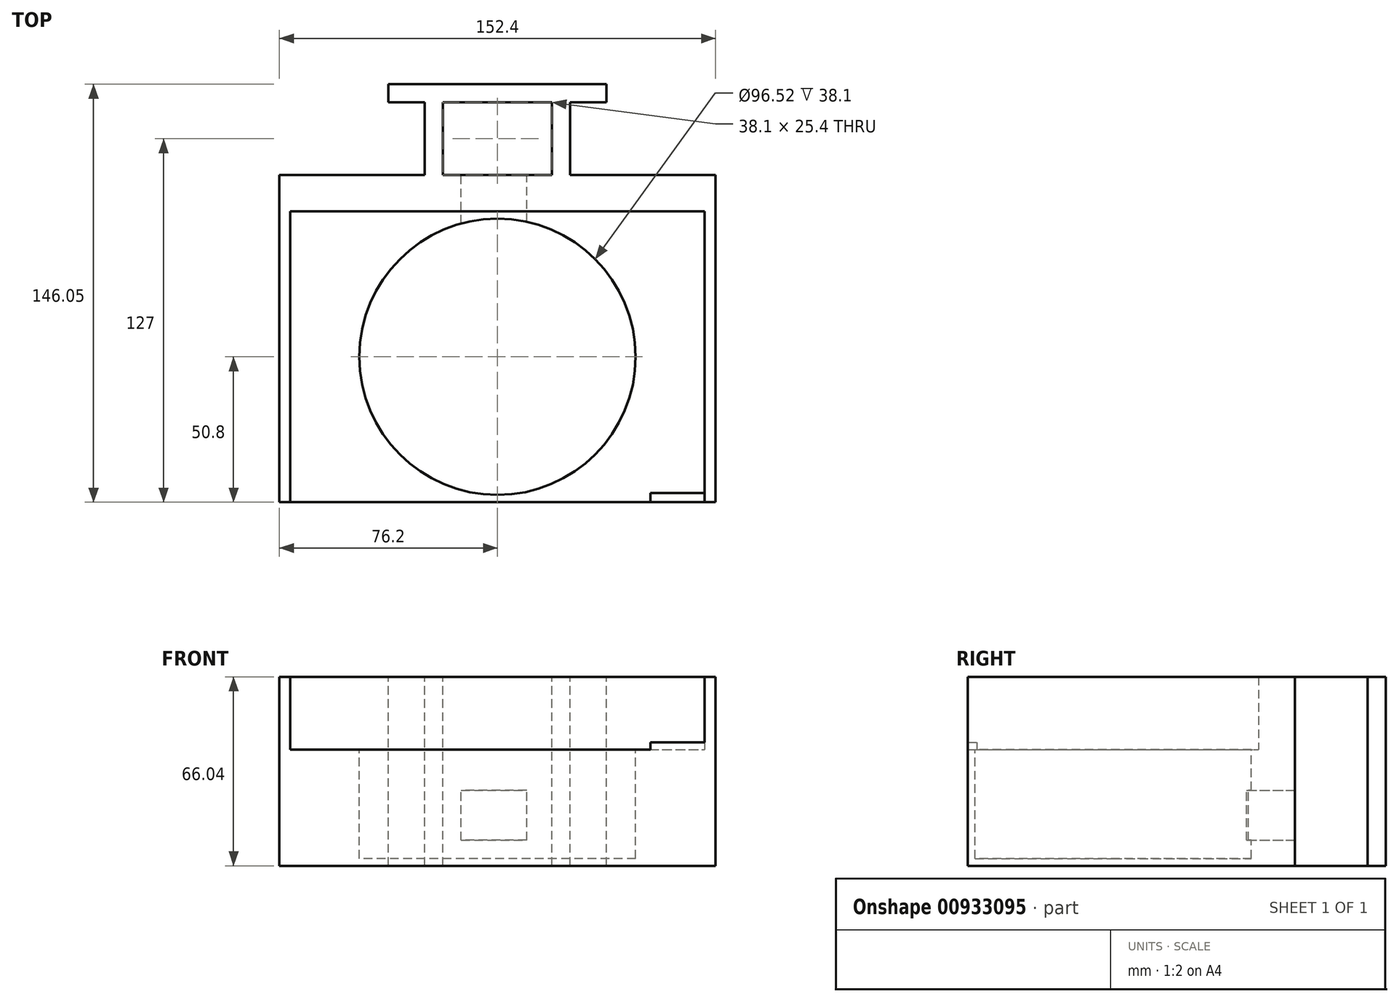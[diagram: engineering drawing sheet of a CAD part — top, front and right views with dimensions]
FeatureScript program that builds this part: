
annotation { "Feature Type Name" : "Feature", "Feature Type Description" : "" }
export const myFeature = defineFeature(function(context is Context, id is Id, definition is map)
    precondition{}
    {
        {
            var Q0;
            Q0=qCreatedBy(makeId("Top.planeOp"),FACE);
            var sketch = newSketch(context, id + "F0", { "sketchPlane" : qUnion([Q0])});
            skLineSegment(sketch, "E0.bottom", {"start": v(-76.2, 57.15) * mm, "end": v(76.2, 57.15) * mm});
            skLineSegment(sketch, "E0.top", {"start": v(-76.2, -57.15) * mm, "end": v(76.2, -57.15) * mm});
            skLineSegment(sketch, "E0.left", {"start": v(-76.2, 57.15) * mm, "end": v(-76.2, -57.15) * mm});
            skLineSegment(sketch, "E0.right", {"start": v(76.2, 57.15) * mm, "end": v(76.2, -57.15) * mm});
            skSolve(sketch);
        }
        {
            var Q0;
            Q0=makeQuery(id+"F0.imprint","IMPRINT",FACE,{"disambiguationData":[TD([[makeQuery(id+"F0.imprint","IMPRINT",EDGE,{"derivedFrom":sQuery(id+"F0.wireOp",EDGE,"E0.bottom")}),-1.0]])]});
            extrude(context, id + "F1", {"entities" : qUnion([Q0]), "depth" : 40.64 * mm, "offsetDistance" : 25.4 * mm});
        }
        {
            var Q0;
            Q0=makeQuery(id+"F1.opExtrude","CAP_FACE",FACE,{"disambiguationData":[OSD([sQuery(id+"F0.wireOp",EDGE,"E0.bottom"),sQuery(id+"F0.wireOp",EDGE,"E0.top"),sQuery(id+"F0.wireOp",EDGE,"E0.left"),sQuery(id+"F0.wireOp",EDGE,"E0.right")])],"isStart":false});
            var sketch = newSketch(context, id + "F2", { "sketchPlane" : qUnion([Q0])});
            skLineSegment(sketch, "E1.trimOffspring", {"start": v(-72.4, 44.45) * mm, "end": v(72.4, 44.45) * mm});
            skLineSegment(sketch, "E2", {"start": v(76.2, 57.15) * mm, "end": v(-76.2, 57.15) * mm});
            skLineSegment(sketch, "E3.bottom", {"start": v(76.2, -57.15) * mm, "end": v(72.4, -57.15) * mm});
            skLineSegment(sketch, "E3.left", {"start": v(76.2, -57.15) * mm, "end": v(76.2, 57.15) * mm});
            skLineSegment(sketch, "E4.bottom", {"start": v(-76.2, -57.15) * mm, "end": v(-72.4, -57.15) * mm});
            skLineSegment(sketch, "E4.left", {"start": v(-76.2, -57.15) * mm, "end": v(-76.2, 57.15) * mm});
            skLineSegment(sketch, "E4.right", {"start": v(-72.4, -57.15) * mm, "end": v(-72.4, 44.45) * mm});
            skLineSegment(sketch, "E5", {"start": v(72.4, -57.15) * mm, "end": v(72.4, 44.45) * mm});
            skSolve(sketch);
        }
        {
            var Q0;
            {var subQ0=sQuery(id+"F2.wireOp",EDGE,"OgKXzPdw-eDsp-d21L-xpKS-83sbPqBPL3Dp.bottom");Q0=makeQuery(id+"F2.imprint","IMPRINT",FACE,{"disambiguationData":[TD([[makeQuery(id+"F2.imprint","IMPRINT",EDGE,{"derivedFrom":subQ0}),1.0]])]});}
            var Q1;
            {var subQ0=sQuery(id+"F2.wireOp",EDGE,"E1.trimOffspring");Q1=makeQuery(id+"F2.imprint","IMPRINT",FACE,{"disambiguationData":[TD([[makeQuery(id+"F2.imprint","IMPRINT",EDGE,{"derivedFrom":subQ0}),1.0]])]});}
            var Q2;
            {var subQ0=sQuery(id+"F2.wireOp",EDGE,"0cbdea43-ffa5-4f05-8e79-97b593feb2ee.trimOffspring");Q2=makeQuery(id+"F2.imprint","IMPRINT",FACE,{"disambiguationData":[TD([[makeQuery(id+"F2.imprint","IMPRINT",EDGE,{"derivedFrom":subQ0}),-1.0]])]});}
            var Q3;
            {var subQ0=sQuery(id+"F2.wireOp",EDGE,"OgKXzPdw-eDsp-d21L-xpKS-83sbPqBPL3Dp.top");Q3=makeQuery(id+"F2.imprint","IMPRINT",FACE,{"disambiguationData":[TD([[makeQuery(id+"F2.imprint","IMPRINT",EDGE,{"derivedFrom":subQ0}),-1.0]])]});}
            extrude(context, id + "F3", {"entities" : qUnion([Q0, Q1, Q2, Q3]), "operationType" : NewBodyOperationType.ADD, "depth" : 25.4 * mm, "offsetDistance" : 25.4 * mm});
        }
        {
            var Q0;
            Q0=makeQuery(id+"F1.opExtrude","CAP_FACE",FACE,{"disambiguationData":[OSD([sQuery(id+"F0.wireOp",EDGE,"E0.bottom"),sQuery(id+"F0.wireOp",EDGE,"E0.top"),sQuery(id+"F0.wireOp",EDGE,"E0.left"),sQuery(id+"F0.wireOp",EDGE,"E0.right")])],"isStart":false});
            var sketch = newSketch(context, id + "F4", { "sketchPlane" : qUnion([Q0])});
            skCircle(sketch, "E6", {"center": v(0, -6.35) * mm, "radius": 48.26 * mm});
            skSolve(sketch);
        }
        {
            var Q0;
            Q0=qSketchRegion(id+"F4",true);
            extrude(context, id + "F5", {"entities" : qUnion([Q0]), "operationType" : NewBodyOperationType.REMOVE, "oppositeDirection" : true, "depth" : 38.1 * mm, "offsetDistance" : 25.4 * mm});
        }
        {
            var Q0;
            Q0=makeQuery(id+"F3.opExtrude","CAP_FACE",FACE,{"disambiguationData":[OSD([sQuery(id+"F2.wireOp",EDGE,"E1.trimOffspring"),sQuery(id+"F2.wireOp",EDGE,"E2"),sQuery(id+"F2.wireOp",EDGE,"E3.bottom"),sQuery(id+"F2.wireOp",EDGE,"E3.left"),sQuery(id+"F2.wireOp",EDGE,"E4.bottom"),sQuery(id+"F2.wireOp",EDGE,"E4.left"),sQuery(id+"F2.wireOp",EDGE,"E4.right"),sQuery(id+"F2.wireOp",EDGE,"E5")])],"isStart":false});
            var sketch = newSketch(context, id + "F6", { "sketchPlane" : qUnion([Q0])});
            skLineSegment(sketch, "E7.bottom", {"start": v(-25.4, 57.15) * mm, "end": v(25.4, 57.15) * mm});
            skLineSegment(sketch, "E7.top", {"start": v(-25.4, 82.55) * mm, "end": v(25.4, 82.55) * mm});
            skLineSegment(sketch, "E7.left", {"start": v(-25.4, 57.15) * mm, "end": v(-25.4, 82.55) * mm});
            skLineSegment(sketch, "E7.right", {"start": v(25.4, 57.15) * mm, "end": v(25.4, 82.55) * mm});
            skLineSegment(sketch, "E8.bottom", {"start": v(-38.1, 88.9) * mm, "end": v(38.1, 88.9) * mm});
            skLineSegment(sketch, "E8.top", {"start": v(-38.1, 82.55) * mm, "end": v(38.1, 82.55) * mm});
            skLineSegment(sketch, "E8.left", {"start": v(-38.1, 88.9) * mm, "end": v(-38.1, 82.55) * mm});
            skLineSegment(sketch, "E8.right", {"start": v(38.1, 88.9) * mm, "end": v(38.1, 82.55) * mm});
            skSolve(sketch);
        }
        {
            var Q0;
            Q0=makeQuery(id+"F6.imprint","IMPRINT",FACE,{"disambiguationData":[TD([[makeQuery(id+"F6.imprint","IMPRINT",EDGE,{"derivedFrom":sQuery(id+"F6.wireOp",EDGE,"E7.bottom")}),1.0]])]});
            var Q1;
            Q1=makeQuery(id+"F6.imprint","IMPRINT",FACE,{"disambiguationData":[TD([[makeQuery(id+"F6.imprint","IMPRINT",EDGE,{"derivedFrom":sQuery(id+"F6.wireOp",EDGE,"E8.bottom")}),-1.0]])]});
            extrude(context, id + "F7", {"entities" : qUnion([Q0, Q1]), "operationType" : NewBodyOperationType.ADD, "oppositeDirection" : true, "depth" : 66.04 * mm, "offsetDistance" : 25.4 * mm});
        }
        {
            var Q0;
            Q0=makeQuery(id+"F7.boolean.opBoolean","MERGE",FACE,{"derivedFrom":[makeQuery(id+"F3.opExtrude","CAP_FACE",FACE,{"disambiguationData":[OSD([sQuery(id+"F2.wireOp",EDGE,"E1.trimOffspring"),sQuery(id+"F2.wireOp",EDGE,"E2"),sQuery(id+"F2.wireOp",EDGE,"E3.bottom"),sQuery(id+"F2.wireOp",EDGE,"E3.left"),sQuery(id+"F2.wireOp",EDGE,"E4.bottom"),sQuery(id+"F2.wireOp",EDGE,"E4.left"),sQuery(id+"F2.wireOp",EDGE,"E4.right"),sQuery(id+"F2.wireOp",EDGE,"E5")])],"isStart":false}),makeQuery(id+"F7.opExtrude","CAP_FACE",FACE,{"disambiguationData":[OSD([sQuery(id+"F6.wireOp",EDGE,"E7.bottom"),sQuery(id+"F6.wireOp",EDGE,"E7.left"),sQuery(id+"F6.wireOp",EDGE,"E7.right"),sQuery(id+"F6.wireOp",EDGE,"E8.bottom"),sQuery(id+"F6.wireOp",EDGE,"E8.top"),sQuery(id+"F6.wireOp",EDGE,"E8.left"),sQuery(id+"F6.wireOp",EDGE,"E8.right")])],"isStart":true})]});
            var sketch = newSketch(context, id + "F8", { "sketchPlane" : qUnion([Q0])});
            skLineSegment(sketch, "E9.bottom", {"start": v(-19.05, 82.55) * mm, "end": v(19.05, 82.55) * mm});
            skLineSegment(sketch, "E9.top", {"start": v(-19.05, 57.15) * mm, "end": v(19.05, 57.15) * mm});
            skLineSegment(sketch, "E9.left", {"start": v(-19.05, 82.55) * mm, "end": v(-19.05, 57.15) * mm});
            skLineSegment(sketch, "E9.right", {"start": v(19.05, 82.55) * mm, "end": v(19.05, 57.15) * mm});
            skSolve(sketch);
        }
        {
            var Q0;
            Q0=makeQuery(id+"F8.imprint","IMPRINT",FACE,{"disambiguationData":[TD([[makeQuery(id+"F8.imprint","IMPRINT",EDGE,{"derivedFrom":sQuery(id+"F8.wireOp",EDGE,"E9.bottom")}),-1.0]])]});
            extrude(context, id + "F9", {"entities" : qUnion([Q0]), "operationType" : NewBodyOperationType.REMOVE, "oppositeDirection" : true, "depth" : 66.04 * mm, "offsetDistance" : 25.4 * mm});
        }
        {
            var Q0;
            Q0=makeQuery(id+"F1.opExtrude","CAP_FACE",FACE,{"disambiguationData":[OSD([sQuery(id+"F0.wireOp",EDGE,"E0.bottom"),sQuery(id+"F0.wireOp",EDGE,"E0.top"),sQuery(id+"F0.wireOp",EDGE,"E0.left"),sQuery(id+"F0.wireOp",EDGE,"E0.right")])],"isStart":false});
            var sketch = newSketch(context, id + "F10", { "sketchPlane" : qUnion([Q0])});
            skLineSegment(sketch, "E10.bottom", {"start": v(-72.4, -57.15) * mm, "end": v(72.4, -57.15) * mm});
            skLineSegment(sketch, "E10.top", {"start": v(-72.4, -53.97) * mm, "end": v(27.98, -53.97) * mm});
            skLineSegment(sketch, "E10.left", {"start": v(-72.4, -57.15) * mm, "end": v(-72.4, -53.97) * mm});
            skLineSegment(sketch, "E10.right", {"start": v(72.4, -57.15) * mm, "end": v(72.4, -53.97) * mm});
            skLineSegment(sketch, "E11", {"start": v(27.98, -53.97) * mm, "end": v(27.98, -57.15) * mm});
            skLineSegment(sketch, "E12", {"start": v(53.38, -57.15) * mm, "end": v(53.38, -53.97) * mm});
            skLineSegment(sketch, "E13.trimOffspring", {"start": v(53.38, -53.97) * mm, "end": v(72.4, -53.97) * mm});
            skSolve(sketch);
        }
        {
            var Q0;
            Q0=makeQuery(id+"F10.imprint","IMPRINT",FACE,{"disambiguationData":[TD([[makeQuery(id+"F10.imprint","IMPRINT",EDGE,{"derivedFrom":sQuery(id+"F10.wireOp",EDGE,"E10.bottom")}),1.0]])]});
            extrude(context, id + "F11", {"entities" : qUnion([Q0]), "operationType" : NewBodyOperationType.ADD, "depth" : 2.54 * mm, "offsetDistance" : 25.4 * mm});
        }
        {
            var Q0;
            Q0=makeQuery(id+"F9.boolean.opBoolean","COPY",FACE,{"derivedFrom":makeQuery(id+"F9.opExtrude","SWEPT_FACE",FACE,{"disambiguationData":[OSD([sQuery(id+"F8.wireOp",EDGE,"E9.top")])]})});
            var sketch = newSketch(context, id + "F12", { "sketchPlane" : qUnion([Q0])});
            skLineSegment(sketch, "E14.bottom", {"start": v(-10.19, 8.94) * mm, "end": v(12.69, 8.94) * mm});
            skLineSegment(sketch, "E14.top", {"start": v(-10.19, 26.36) * mm, "end": v(12.69, 26.36) * mm});
            skLineSegment(sketch, "E14.left", {"start": v(-10.19, 8.94) * mm, "end": v(-10.19, 26.36) * mm});
            skLineSegment(sketch, "E14.right", {"start": v(12.69, 8.94) * mm, "end": v(12.69, 26.36) * mm});
            skSolve(sketch);
        }
        {
            var Q0;
            Q0 = qSketchRegion(id + "F12", true);
            extrude(context, id + "F13", {"entities" : qUnion([Q0]), "operationType" : NewBodyOperationType.REMOVE, "oppositeDirection" : true, "depth" : 25.4 * mm, "offsetDistance" : 25.4 * mm});
        }
    });
